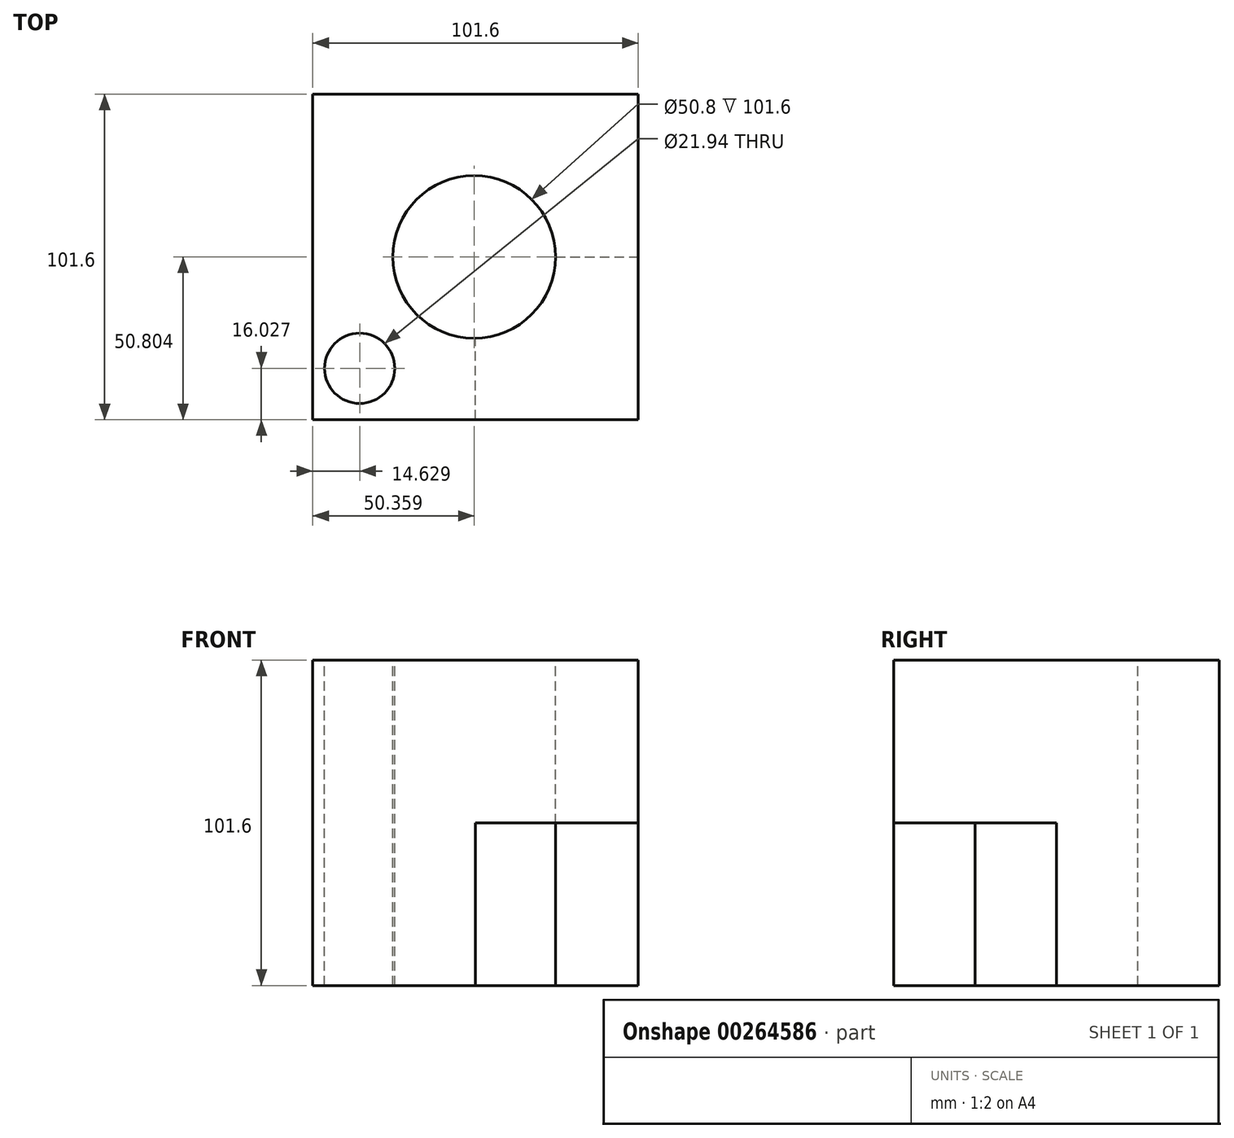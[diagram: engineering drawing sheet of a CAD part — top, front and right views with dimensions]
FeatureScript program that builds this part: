
annotation { "Feature Type Name" : "Feature", "Feature Type Description" : "" }
export const myFeature = defineFeature(function(context is Context, id is Id, definition is map)
    precondition{}
    {
        {
            var Q0;
            Q0=qCreatedBy(makeId("Front.planeOp"),FACE);
            var sketch = newSketch(context, id + "F0", { "sketchPlane" : qUnion([Q0])});
            skLineSegment(sketch, "E0.bottom", {"start": v(0, 0) * mm, "end": v(-101.6, 0) * mm});
            skLineSegment(sketch, "E0.top", {"start": v(0, 101.6) * mm, "end": v(-101.6, 101.6) * mm});
            skLineSegment(sketch, "E0.left", {"start": v(0, 0) * mm, "end": v(0, 101.6) * mm});
            skLineSegment(sketch, "E0.right", {"start": v(-101.6, 0) * mm, "end": v(-101.6, 101.6) * mm});
            skSolve(sketch);
        }
        {
            var Q0;
            Q0=makeQuery(id+"F0.imprint","IMPRINT",FACE,{"disambiguationData":[TD([[makeQuery(id+"F0.imprint","IMPRINT",EDGE,{"derivedFrom":sQuery(id+"F0.wireOp",EDGE,"E0.bottom")}),-1.0]])]});
            extrude(context, id + "F1", {"entities" : qUnion([Q0]), "depth" : 101.6 * mm});
        }
        {
            var Q0;
            Q0=makeQuery(id+"F1.opExtrude","SWEPT_FACE",FACE,{"disambiguationData":[OSD([sQuery(id+"F0.wireOp",EDGE,"E0.top")])]});
            var sketch = newSketch(context, id + "F2", { "sketchPlane" : qUnion([Q0])});
            skCircle(sketch, "E1", {"center": v(-51.24, -50.8) * mm, "radius": 25.4 * mm});
            skSolve(sketch);
        }
        {
            var Q0;
            Q0 = qSketchRegion(id + "F2", true);
            extrude(context, id + "F3", {"entities" : qUnion([Q0]), "operationType" : NewBodyOperationType.REMOVE, "oppositeDirection" : true, "depth" : 101.6 * mm});
        }
        {
            var Q0;
            Q0=makeQuery(id+"F1.opExtrude","SWEPT_FACE",FACE,{"disambiguationData":[OSD([sQuery(id+"F0.wireOp",EDGE,"E0.left")])]});
            var sketch = newSketch(context, id + "F4", { "sketchPlane" : qUnion([Q0])});
            skLineSegment(sketch, "E2.bottom", {"start": v(-101.6, 0) * mm, "end": v(-50.8, 0) * mm});
            skLineSegment(sketch, "E2.top", {"start": v(-101.6, 50.8) * mm, "end": v(-50.8, 50.8) * mm});
            skLineSegment(sketch, "E2.left", {"start": v(-101.6, 0) * mm, "end": v(-101.6, 50.8) * mm});
            skLineSegment(sketch, "E2.right", {"start": v(-50.8, 0) * mm, "end": v(-50.8, 50.8) * mm});
            skSolve(sketch);
        }
        {
            var Q0;
            Q0 = qSketchRegion(id + "F4", true);
            extrude(context, id + "F5", {"entities" : qUnion([Q0]), "operationType" : NewBodyOperationType.REMOVE, "oppositeDirection" : true, "depth" : 50.8 * mm});
        }
        {
            var Q0;
            Q0=makeQuery(id+"F1.opExtrude","SWEPT_FACE",FACE,{"disambiguationData":[OSD([sQuery(id+"F0.wireOp",EDGE,"E0.top")])]});
            var sketch = newSketch(context, id + "F6", { "sketchPlane" : qUnion([Q0])});
            skCircle(sketch, "E3", {"center": v(-86.97, -85.57) * mm, "radius": 10.97 * mm});
            skSolve(sketch);
        }
        {
            var Q0;
            Q0 = qSketchRegion(id + "F6", true);
            extrude(context, id + "F7", {"entities" : qUnion([Q0]), "operationType" : NewBodyOperationType.REMOVE, "oppositeDirection" : true, "depth" : 101.6 * mm});
        }
    });
